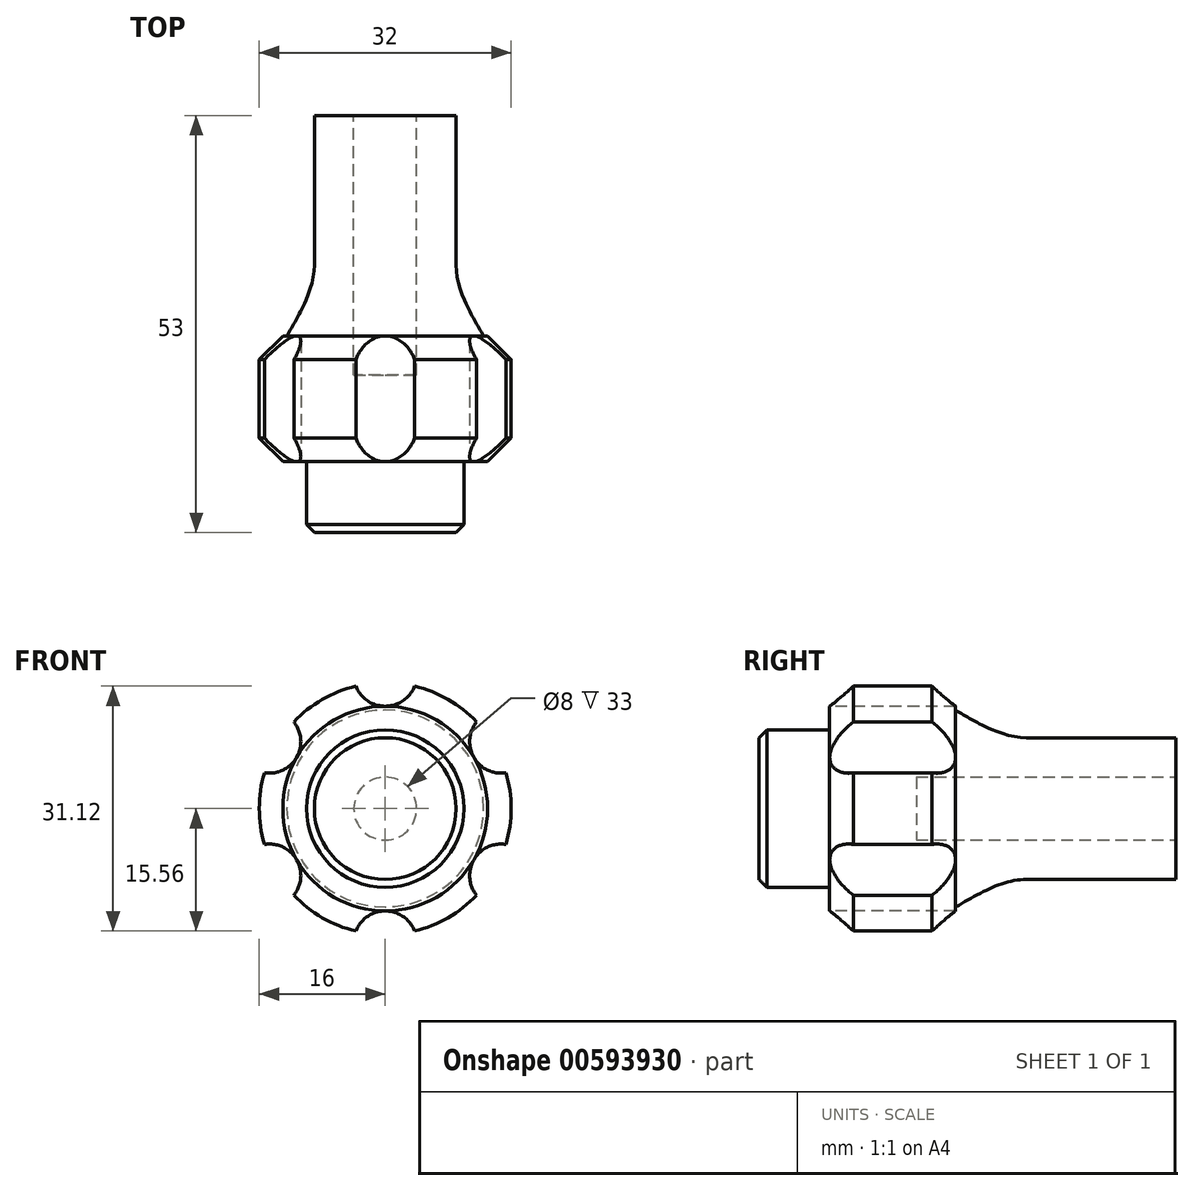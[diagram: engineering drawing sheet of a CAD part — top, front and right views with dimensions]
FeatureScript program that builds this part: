
annotation { "Feature Type Name" : "Feature", "Feature Type Description" : "" }
export const myFeature = defineFeature(function(context is Context, id is Id, definition is map)
    precondition{}
    {
        {
            var Q0;
            Q0=qCreatedBy(makeId("Front.planeOp"),FACE);
            var sketch = newSketch(context, id + "F0", { "sketchPlane" : qUnion([Q0])});
            skCircle(sketch, "E0", {"center": v(0, 0) * mm, "radius": 9 * mm});
            skSolve(sketch);
        }
        {
            var Q0;
            Q0=makeQuery(id+"F0.imprint","IMPRINT",FACE,{"disambiguationData":[TD([[makeQuery(id+"F0.imprint","IMPRINT",EDGE,{"derivedFrom":sQuery(id+"F0.wireOp",EDGE,"E0")}),1.0]])]});
            extrude(context, id + "F1", {"entities" : qUnion([Q0]), "depth" : 19 * mm, "offsetDistance" : 25 * mm});
        }
        {
            var Q0;
            Q0=makeQuery(id+"F1.opExtrude","CAP_FACE",FACE,{"disambiguationData":[OSD([sQuery(id+"F0.wireOp",EDGE,"E0")])],"isStart":false});
            cPlane(context, id + "F2", {"entities" : qUnion([Q0]), "cplaneType" : CPlaneType.OFFSET, "offset" : 9 * mm, "width" : 150 * mm, "height" : 150 * mm});
        }
        {
            var Q0;
            Q0=qCreatedBy(id+"F2.planeOp",FACE);
            var sketch = newSketch(context, id + "F3", { "sketchPlane" : qUnion([Q0])});
            skCircle(sketch, "E1", {"center": v(0, 0) * mm, "radius": 12.5 * mm});
            skSolve(sketch);
        }
        {
            var Q0;
            Q0=makeQuery(id+"F1.opExtrude","CAP_FACE",FACE,{"disambiguationData":[OSD([sQuery(id+"F0.wireOp",EDGE,"E0")])],"isStart":true});
            var sketch = newSketch(context, id + "F4", { "sketchPlane" : qUnion([Q0])});
            skCircle(sketch, "E2", {"center": v(0, 0) * mm, "radius": 4 * mm});
            skSolve(sketch);
        }
        {
            var Q1;
            Q1=makeQuery(id+"F1.opExtrude","CAP_FACE",FACE,{"disambiguationData":[OSD([sQuery(id+"F0.wireOp",EDGE,"E0")])],"isStart":false});
            var Q2;
            Q2=makeQuery(id+"F3.imprint","IMPRINT",FACE,{"disambiguationData":[TD([[makeQuery(id+"F3.imprint","IMPRINT",EDGE,{"derivedFrom":sQuery(id+"F3.wireOp",EDGE,"E1")}),1.0]])]});
            loft(context, id + "F5", {"operationType" : NewBodyOperationType.ADD, "startCondition" : LoftEndDerivativeType.NORMAL_TO_PROFILE, "startMagnitude" : 1, "sheetProfilesArray" : [{ "sheetProfileEntities" : qUnion([Q1]) }, { "sheetProfileEntities" : qUnion([Q2]) }]});
        }
        {
            var Q0;
            Q0=makeQuery(id+"F5.opLoft","CAP_FACE",FACE,{"disambiguationData":[OSD([makeQuery(id+"F3.imprint","IMPRINT",FACE,{"disambiguationData":[TD([[makeQuery(id+"F3.imprint","IMPRINT",EDGE,{"derivedFrom":sQuery(id+"F3.wireOp",EDGE,"E1")}),1.0]])]})])],"isStart":true});
            var sketch = newSketch(context, id + "F6", { "sketchPlane" : qUnion([Q0])});
            skCircle(sketch, "E3", {"center": v(0, 0) * mm, "radius": 16 * mm});
            skSolve(sketch);
        }
        {
            var Q0;
            Q0=makeQuery(id+"F6.imprint","IMPRINT",FACE,{"disambiguationData":[TD([[makeQuery(id+"F6.imprint","IMPRINT",EDGE,{"derivedFrom":makeQuery(id+"F5.opLoft","MID_CAP_EDGE",EDGE,{"disambiguationData":[OSD([sQuery(id+"F0.wireOp",EDGE,"E0"),sQuery(id+"F3.wireOp",EDGE,"E1")])],"capPos":1.0})}),1.0]])]});
            var Q1;
            Q1=makeQuery(id+"F6.imprint","IMPRINT",FACE,{"disambiguationData":[TD([[makeQuery(id+"F6.imprint","IMPRINT",EDGE,{"derivedFrom":sQuery(id+"F6.wireOp",EDGE,"E3")}),1.0]])]});
            extrude(context, id + "F7", {"entities" : qUnion([Q0, Q1]), "operationType" : NewBodyOperationType.ADD, "depth" : 16 * mm, "offsetDistance" : 25 * mm});
        }
        {
            var Q0;
            Q0=makeQuery(id+"F7.opExtrude","CAP_FACE",FACE,{"disambiguationData":[OSD([sQuery(id+"F6.wireOp",EDGE,"E3")])],"isStart":false});
            var sketch = newSketch(context, id + "F8", { "sketchPlane" : qUnion([Q0])});
            skCircle(sketch, "E4", {"center": v(0, 0) * mm, "radius": 10 * mm});
            skSolve(sketch);
        }
        {
            var Q0;
            Q0=qSketchRegion(id+"F8",true);
            extrude(context, id + "F9", {"entities" : qUnion([Q0]), "operationType" : NewBodyOperationType.ADD, "depth" : 9 * mm, "offsetDistance" : 25 * mm});
        }
        {
            var Q0;
            Q0=makeQuery(id+"F7.opExtrude","CAP_FACE",FACE,{"disambiguationData":[OSD([sQuery(id+"F6.wireOp",EDGE,"E3")])],"isStart":false});
            var sketch = newSketch(context, id + "F10", { "sketchPlane" : qUnion([Q0])});
            skCircle(sketch, "E5.0", {"center": v(0, 0) * mm, "radius": 17 * mm, "construction": true});
            skCircle(sketch, "E6", {"center": v(0, 0) * mm, "radius": 13 * mm, "construction": true});
            skCircle(sketch, "E7", {"center": v(0, 17) * mm, "radius": 4 * mm});
            skCircle(sketch, "E8.1.0", {"center": v(-14.72, 8.5) * mm, "radius": 4 * mm});
            skCircle(sketch, "E8.2.0", {"center": v(-14.72, -8.5) * mm, "radius": 4 * mm});
            skCircle(sketch, "E8.3.0", {"center": v(0, -17) * mm, "radius": 4 * mm});
            skCircle(sketch, "E8.4.0", {"center": v(14.72, -8.5) * mm, "radius": 4 * mm});
            skCircle(sketch, "E8.5.0", {"center": v(14.72, 8.5) * mm, "radius": 4 * mm});
            skSolve(sketch);
        }
        {
            var Q0;
            Q0=makeQuery(id+"F4.imprint","IMPRINT",FACE,{"disambiguationData":[TD([[makeQuery(id+"F4.imprint","IMPRINT",EDGE,{"derivedFrom":sQuery(id+"F4.wireOp",EDGE,"E2")}),1.0]])]});
            extrude(context, id + "F11", {"entities" : qUnion([Q0]), "operationType" : NewBodyOperationType.REMOVE, "oppositeDirection" : true, "depth" : 33 * mm, "offsetDistance" : 25 * mm});
        }
        {
            var Q0;
            Q0=makeQuery(id+"F10.imprint","IMPRINT",FACE,{"disambiguationData":[TD([[makeQuery(id+"F10.imprint","IMPRINT",EDGE,{"derivedFrom":sQuery(id+"F10.wireOp",EDGE,"E7")}),1.0]])]});
            var Q1;
            Q1=makeQuery(id+"F10.imprint","IMPRINT",FACE,{"disambiguationData":[TD([[makeQuery(id+"F10.imprint","IMPRINT",EDGE,{"derivedFrom":sQuery(id+"F10.wireOp",EDGE,"E8.1.0")}),1.0]])]});
            var Q2;
            Q2=makeQuery(id+"F10.imprint","IMPRINT",FACE,{"disambiguationData":[TD([[makeQuery(id+"F10.imprint","IMPRINT",EDGE,{"derivedFrom":sQuery(id+"F10.wireOp",EDGE,"E8.2.0")}),1.0]])]});
            var Q3;
            Q3=makeQuery(id+"F10.imprint","IMPRINT",FACE,{"disambiguationData":[TD([[makeQuery(id+"F10.imprint","IMPRINT",EDGE,{"derivedFrom":sQuery(id+"F10.wireOp",EDGE,"E8.3.0")}),1.0]])]});
            var Q4;
            Q4=makeQuery(id+"F10.imprint","IMPRINT",FACE,{"disambiguationData":[TD([[makeQuery(id+"F10.imprint","IMPRINT",EDGE,{"derivedFrom":sQuery(id+"F10.wireOp",EDGE,"E8.4.0")}),1.0]])]});
            var Q5;
            Q5=makeQuery(id+"F10.imprint","IMPRINT",FACE,{"disambiguationData":[TD([[makeQuery(id+"F10.imprint","IMPRINT",EDGE,{"derivedFrom":sQuery(id+"F10.wireOp",EDGE,"E8.5.0")}),1.0]])]});
            extrude(context, id + "F12", {"entities" : qUnion([Q0, Q1, Q2, Q3, Q4, Q5]), "operationType" : NewBodyOperationType.REMOVE, "endBound" : BoundingType.THROUGH_ALL, "oppositeDirection" : true, "depth" : 25 * mm, "offsetDistance" : 25 * mm});
        }
        {
            var Q0;
            Q0=makeQuery(id+"F9.opExtrude","CAP_EDGE",EDGE,{"disambiguationData":[OSD([sQuery(id+"F8.wireOp",EDGE,"E4")])],"isStart":true});
            var Q1;
            {var subQ0=sQuery(id+"F6.wireOp",EDGE,"E3");Q1=makeQuery(id+"F12.boolean.opBoolean","SPLIT",EDGE,{"disambiguationData":[TD([makeQuery(id+"F7.opExtrude","SWEPT_FACE",FACE,{"disambiguationData":[OSD([subQ0])]}),makeQuery(id+"F7.opExtrude","CAP_FACE",FACE,{"disambiguationData":[OSD([subQ0])],"isStart":false}),makeQuery(id+"F12.opExtrude","SWEPT_FACE",FACE,{"disambiguationData":[OSD([sQuery(id+"F10.wireOp",EDGE,"E8.2.0")])]}),makeQuery(id+"F12.opExtrude","SWEPT_FACE",FACE,{"disambiguationData":[OSD([sQuery(id+"F10.wireOp",EDGE,"E8.3.0")])]})])],"derivedFrom":makeQuery(id+"F7.opExtrude","CAP_EDGE",EDGE,{"disambiguationData":[OSD([subQ0])],"isStart":false})});}
            var Q2;
            {var subQ0=sQuery(id+"F6.wireOp",EDGE,"E3");Q2=makeQuery(id+"F12.boolean.opBoolean","SPLIT",EDGE,{"disambiguationData":[TD([makeQuery(id+"F7.opExtrude","SWEPT_FACE",FACE,{"disambiguationData":[OSD([subQ0])]}),makeQuery(id+"F7.opExtrude","CAP_FACE",FACE,{"disambiguationData":[OSD([subQ0])],"isStart":false}),makeQuery(id+"F12.opExtrude","SWEPT_FACE",FACE,{"disambiguationData":[OSD([sQuery(id+"F10.wireOp",EDGE,"E8.1.0")])]}),makeQuery(id+"F12.opExtrude","SWEPT_FACE",FACE,{"disambiguationData":[OSD([sQuery(id+"F10.wireOp",EDGE,"E8.2.0")])]})])],"derivedFrom":makeQuery(id+"F7.opExtrude","CAP_EDGE",EDGE,{"disambiguationData":[OSD([subQ0])],"isStart":false})});}
            var Q3;
            {var subQ0=sQuery(id+"F6.wireOp",EDGE,"E3");Q3=makeQuery(id+"F12.boolean.opBoolean","SPLIT",EDGE,{"disambiguationData":[TD([makeQuery(id+"F7.opExtrude","SWEPT_FACE",FACE,{"disambiguationData":[OSD([subQ0])]}),makeQuery(id+"F7.opExtrude","CAP_FACE",FACE,{"disambiguationData":[OSD([subQ0])],"isStart":false}),makeQuery(id+"F12.opExtrude","SWEPT_FACE",FACE,{"disambiguationData":[OSD([sQuery(id+"F10.wireOp",EDGE,"E7")])]}),makeQuery(id+"F12.opExtrude","SWEPT_FACE",FACE,{"disambiguationData":[OSD([sQuery(id+"F10.wireOp",EDGE,"E8.1.0")])]})])],"derivedFrom":makeQuery(id+"F7.opExtrude","CAP_EDGE",EDGE,{"disambiguationData":[OSD([subQ0])],"isStart":false})});}
            var Q4;
            {var subQ0=sQuery(id+"F6.wireOp",EDGE,"E3");Q4=makeQuery(id+"F12.boolean.opBoolean","SPLIT",EDGE,{"disambiguationData":[TD([makeQuery(id+"F7.opExtrude","SWEPT_FACE",FACE,{"disambiguationData":[OSD([subQ0])]}),makeQuery(id+"F7.opExtrude","CAP_FACE",FACE,{"disambiguationData":[OSD([subQ0])],"isStart":false}),makeQuery(id+"F12.opExtrude","SWEPT_FACE",FACE,{"disambiguationData":[OSD([sQuery(id+"F10.wireOp",EDGE,"E7")])]}),makeQuery(id+"F12.opExtrude","SWEPT_FACE",FACE,{"disambiguationData":[OSD([sQuery(id+"F10.wireOp",EDGE,"E8.5.0")])]})])],"derivedFrom":makeQuery(id+"F7.opExtrude","CAP_EDGE",EDGE,{"disambiguationData":[OSD([subQ0])],"isStart":false})});}
            var Q5;
            {var subQ0=sQuery(id+"F6.wireOp",EDGE,"E3");Q5=makeQuery(id+"F12.boolean.opBoolean","SPLIT",EDGE,{"disambiguationData":[TD([makeQuery(id+"F7.opExtrude","SWEPT_FACE",FACE,{"disambiguationData":[OSD([subQ0])]}),makeQuery(id+"F7.opExtrude","CAP_FACE",FACE,{"disambiguationData":[OSD([subQ0])],"isStart":false}),makeQuery(id+"F12.opExtrude","SWEPT_FACE",FACE,{"disambiguationData":[OSD([sQuery(id+"F10.wireOp",EDGE,"E8.4.0")])]}),makeQuery(id+"F12.opExtrude","SWEPT_FACE",FACE,{"disambiguationData":[OSD([sQuery(id+"F10.wireOp",EDGE,"E8.5.0")])]})])],"derivedFrom":makeQuery(id+"F7.opExtrude","CAP_EDGE",EDGE,{"disambiguationData":[OSD([subQ0])],"isStart":false})});}
            var Q6;
            {var subQ0=sQuery(id+"F6.wireOp",EDGE,"E3");Q6=makeQuery(id+"F12.boolean.opBoolean","SPLIT",EDGE,{"disambiguationData":[TD([makeQuery(id+"F7.opExtrude","SWEPT_FACE",FACE,{"disambiguationData":[OSD([subQ0])]}),makeQuery(id+"F7.opExtrude","CAP_FACE",FACE,{"disambiguationData":[OSD([subQ0])],"isStart":false}),makeQuery(id+"F12.opExtrude","SWEPT_FACE",FACE,{"disambiguationData":[OSD([sQuery(id+"F10.wireOp",EDGE,"E8.3.0")])]}),makeQuery(id+"F12.opExtrude","SWEPT_FACE",FACE,{"disambiguationData":[OSD([sQuery(id+"F10.wireOp",EDGE,"E8.4.0")])]})])],"derivedFrom":makeQuery(id+"F7.opExtrude","CAP_EDGE",EDGE,{"disambiguationData":[OSD([subQ0])],"isStart":false})});}
            var Q7;
            {var subQ0=sQuery(id+"F6.wireOp",EDGE,"E3");Q7=makeQuery(id+"F12.boolean.opBoolean","SPLIT",EDGE,{"disambiguationData":[TD([makeQuery(id+"F7.opExtrude","SWEPT_FACE",FACE,{"disambiguationData":[OSD([subQ0])]}),makeQuery(id+"F7.opExtrude","CAP_FACE",FACE,{"disambiguationData":[OSD([subQ0])],"isStart":true}),makeQuery(id+"F12.opExtrude","SWEPT_FACE",FACE,{"disambiguationData":[OSD([sQuery(id+"F10.wireOp",EDGE,"E8.1.0")])]}),makeQuery(id+"F12.opExtrude","SWEPT_FACE",FACE,{"disambiguationData":[OSD([sQuery(id+"F10.wireOp",EDGE,"E8.2.0")])]})])],"derivedFrom":makeQuery(id+"F7.opExtrude","CAP_EDGE",EDGE,{"disambiguationData":[OSD([subQ0])],"isStart":true})});}
            var Q8;
            {var subQ0=sQuery(id+"F6.wireOp",EDGE,"E3");Q8=makeQuery(id+"F12.boolean.opBoolean","SPLIT",EDGE,{"disambiguationData":[TD([makeQuery(id+"F7.opExtrude","SWEPT_FACE",FACE,{"disambiguationData":[OSD([subQ0])]}),makeQuery(id+"F7.opExtrude","CAP_FACE",FACE,{"disambiguationData":[OSD([subQ0])],"isStart":true}),makeQuery(id+"F12.opExtrude","SWEPT_FACE",FACE,{"disambiguationData":[OSD([sQuery(id+"F10.wireOp",EDGE,"E7")])]}),makeQuery(id+"F12.opExtrude","SWEPT_FACE",FACE,{"disambiguationData":[OSD([sQuery(id+"F10.wireOp",EDGE,"E8.1.0")])]})])],"derivedFrom":makeQuery(id+"F7.opExtrude","CAP_EDGE",EDGE,{"disambiguationData":[OSD([subQ0])],"isStart":true})});}
            var Q9;
            {var subQ0=sQuery(id+"F6.wireOp",EDGE,"E3");Q9=makeQuery(id+"F12.boolean.opBoolean","SPLIT",EDGE,{"disambiguationData":[TD([makeQuery(id+"F7.opExtrude","SWEPT_FACE",FACE,{"disambiguationData":[OSD([subQ0])]}),makeQuery(id+"F7.opExtrude","CAP_FACE",FACE,{"disambiguationData":[OSD([subQ0])],"isStart":true}),makeQuery(id+"F12.opExtrude","SWEPT_FACE",FACE,{"disambiguationData":[OSD([sQuery(id+"F10.wireOp",EDGE,"E8.2.0")])]}),makeQuery(id+"F12.opExtrude","SWEPT_FACE",FACE,{"disambiguationData":[OSD([sQuery(id+"F10.wireOp",EDGE,"E8.3.0")])]})])],"derivedFrom":makeQuery(id+"F7.opExtrude","CAP_EDGE",EDGE,{"disambiguationData":[OSD([subQ0])],"isStart":true})});}
            var Q10;
            {var subQ0=sQuery(id+"F6.wireOp",EDGE,"E3");Q10=makeQuery(id+"F12.boolean.opBoolean","SPLIT",EDGE,{"disambiguationData":[TD([makeQuery(id+"F7.opExtrude","SWEPT_FACE",FACE,{"disambiguationData":[OSD([subQ0])]}),makeQuery(id+"F7.opExtrude","CAP_FACE",FACE,{"disambiguationData":[OSD([subQ0])],"isStart":true}),makeQuery(id+"F12.opExtrude","SWEPT_FACE",FACE,{"disambiguationData":[OSD([sQuery(id+"F10.wireOp",EDGE,"E8.3.0")])]}),makeQuery(id+"F12.opExtrude","SWEPT_FACE",FACE,{"disambiguationData":[OSD([sQuery(id+"F10.wireOp",EDGE,"E8.4.0")])]})])],"derivedFrom":makeQuery(id+"F7.opExtrude","CAP_EDGE",EDGE,{"disambiguationData":[OSD([subQ0])],"isStart":true})});}
            var Q11;
            {var subQ0=sQuery(id+"F6.wireOp",EDGE,"E3");Q11=makeQuery(id+"F12.boolean.opBoolean","SPLIT",EDGE,{"disambiguationData":[TD([makeQuery(id+"F7.opExtrude","SWEPT_FACE",FACE,{"disambiguationData":[OSD([subQ0])]}),makeQuery(id+"F7.opExtrude","CAP_FACE",FACE,{"disambiguationData":[OSD([subQ0])],"isStart":true}),makeQuery(id+"F12.opExtrude","SWEPT_FACE",FACE,{"disambiguationData":[OSD([sQuery(id+"F10.wireOp",EDGE,"E8.4.0")])]}),makeQuery(id+"F12.opExtrude","SWEPT_FACE",FACE,{"disambiguationData":[OSD([sQuery(id+"F10.wireOp",EDGE,"E8.5.0")])]})])],"derivedFrom":makeQuery(id+"F7.opExtrude","CAP_EDGE",EDGE,{"disambiguationData":[OSD([subQ0])],"isStart":true})});}
            var Q12;
            {var subQ0=sQuery(id+"F6.wireOp",EDGE,"E3");Q12=makeQuery(id+"F12.boolean.opBoolean","SPLIT",EDGE,{"disambiguationData":[TD([makeQuery(id+"F7.opExtrude","SWEPT_FACE",FACE,{"disambiguationData":[OSD([subQ0])]}),makeQuery(id+"F7.opExtrude","CAP_FACE",FACE,{"disambiguationData":[OSD([subQ0])],"isStart":true}),makeQuery(id+"F12.opExtrude","SWEPT_FACE",FACE,{"disambiguationData":[OSD([sQuery(id+"F10.wireOp",EDGE,"E7")])]}),makeQuery(id+"F12.opExtrude","SWEPT_FACE",FACE,{"disambiguationData":[OSD([sQuery(id+"F10.wireOp",EDGE,"E8.5.0")])]})])],"derivedFrom":makeQuery(id+"F7.opExtrude","CAP_EDGE",EDGE,{"disambiguationData":[OSD([subQ0])],"isStart":true})});}
            chamfer(context, id + "F13", {"entities" : qUnion([Q0, Q1, Q2, Q3, Q4, Q5, Q6, Q7, Q8, Q9, Q10, Q11, Q12]), "width" : 3 * mm, "tangentPropagation" : true});
        }
        {
            var Q0;
            Q0=makeQuery(id+"F9.opExtrude","CAP_EDGE",EDGE,{"disambiguationData":[OSD([sQuery(id+"F8.wireOp",EDGE,"E4")])],"isStart":false});
            chamfer(context, id + "F14", {"entities" : qUnion([Q0]), "width" : 1 * mm, "tangentPropagation" : true});
        }
    });
